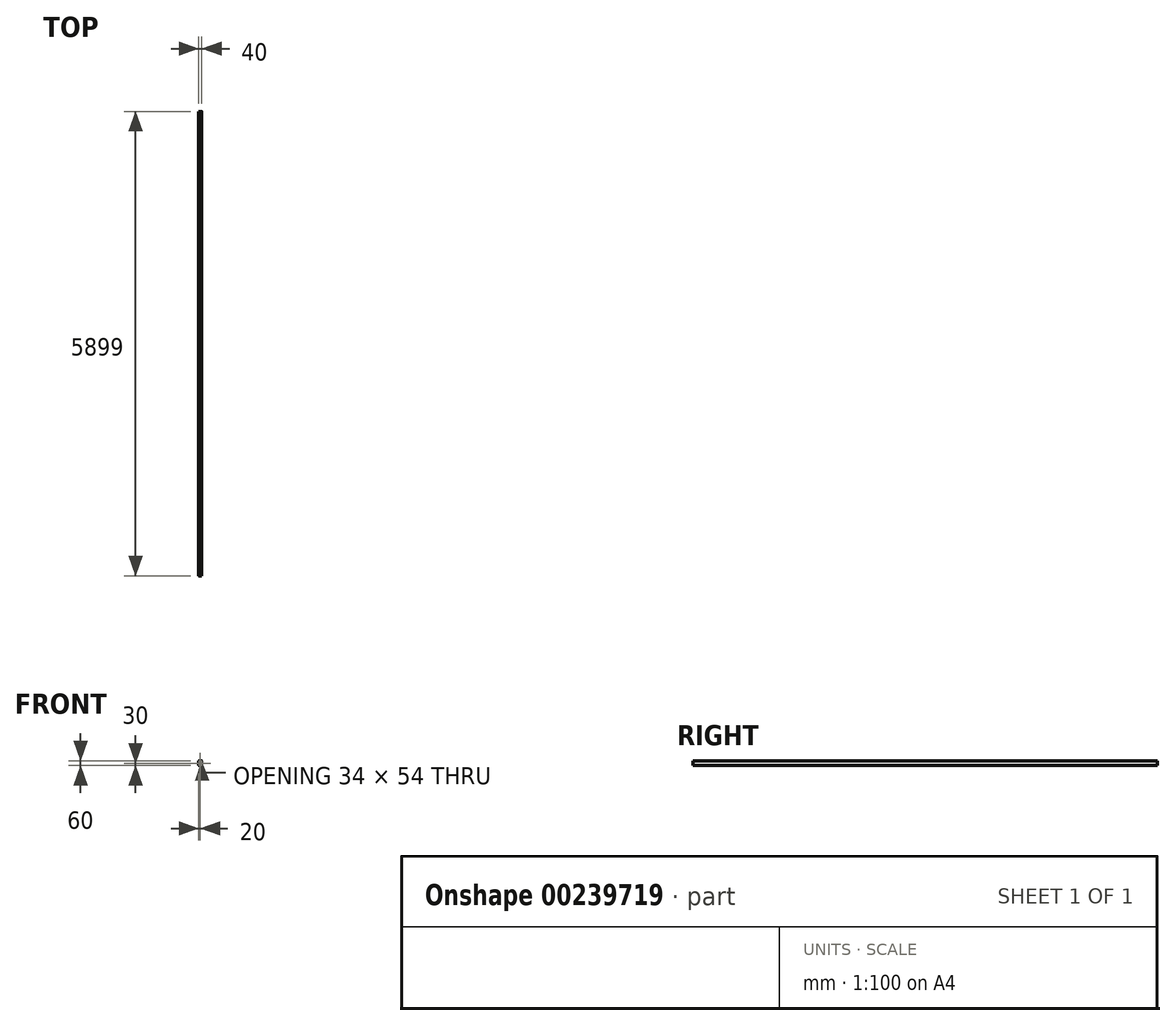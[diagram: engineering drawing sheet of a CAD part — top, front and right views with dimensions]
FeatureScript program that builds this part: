
annotation { "Feature Type Name" : "Feature", "Feature Type Description" : "" }
export const myFeature = defineFeature(function(context is Context, id is Id, definition is map)
    precondition{}
    {
        {
            var Q0;
            Q0=qCreatedBy(makeId("Front.planeOp"),FACE);
            var sketch = newSketch(context, id + "F0", { "sketchPlane" : qUnion([Q0])});
            skLineSegment(sketch, "E0.bottom", {"start": v(16, 30) * mm, "end": v(-16, 30) * mm});
            skLineSegment(sketch, "E0.top", {"start": v(16, -30) * mm, "end": v(-16, -30) * mm});
            skLineSegment(sketch, "E0.left", {"start": v(20, 26) * mm, "end": v(20, -26) * mm});
            skLineSegment(sketch, "E0.right", {"start": v(-20, 26) * mm, "end": v(-20, -26) * mm});
            skPoint(sketch, "E0.middle", {"position": v(0, 0) * mm});
            skPoint(sketch, "E1.visualSharp", {"position": v(-20, 30) * mm});
            skArc(sketch, "E1.filletArc", {"start": v(-16, 30) * mm, "mid": v(-18.83, 28.83) * mm, "end": v(-20, 26) * mm});
            skPoint(sketch, "E2.visualSharp", {"position": v(20, 30) * mm});
            skArc(sketch, "E2.filletArc", {"start": v(20, 26) * mm, "mid": v(18.83, 28.83) * mm, "end": v(16, 30) * mm});
            skPoint(sketch, "E3.visualSharp", {"position": v(20, -30) * mm});
            skArc(sketch, "E3.filletArc", {"start": v(16, -30) * mm, "mid": v(18.83, -28.83) * mm, "end": v(20, -26) * mm});
            skPoint(sketch, "E4.visualSharp", {"position": v(-20, -30) * mm});
            skArc(sketch, "E4.filletArc", {"start": v(-20, -26) * mm, "mid": v(-18.83, -28.83) * mm, "end": v(-16, -30) * mm});
            skLineSegment(sketch, "E5.0", {"start": v(16, 27) * mm, "end": v(-16, 27) * mm});
            skArc(sketch, "E5.1", {"start": v(17, 26) * mm, "mid": v(16.7, 26.7) * mm, "end": v(16, 27) * mm});
            skArc(sketch, "E5.2", {"start": v(-16, 27) * mm, "mid": v(-16.7, 26.7) * mm, "end": v(-17, 26) * mm});
            skLineSegment(sketch, "E5.3", {"start": v(17, 26) * mm, "end": v(17, -26) * mm});
            skLineSegment(sketch, "E5.4", {"start": v(-17, 26) * mm, "end": v(-17, -26) * mm});
            skArc(sketch, "E5.5", {"start": v(-17, -26) * mm, "mid": v(-16.7, -26.7) * mm, "end": v(-16, -27) * mm});
            skLineSegment(sketch, "E5.6", {"start": v(16, -27) * mm, "end": v(-16, -27) * mm});
            skArc(sketch, "E5.7", {"start": v(16, -27) * mm, "mid": v(16.7, -26.7) * mm, "end": v(17, -26) * mm});
            skSolve(sketch);
        }
        {
            var Q0;
            Q0=makeQuery(id+"F0.imprint","IMPRINT",FACE,{"disambiguationData":[TD([[makeQuery(id+"F0.imprint","IMPRINT",EDGE,{"derivedFrom":sQuery(id+"F0.wireOp",EDGE,"E0.bottom")}),1.0]])]});
            extrude(context, id + "F1", {"entities" : qUnion([Q0]), "depth" : 5899 * mm});
        }
    });
